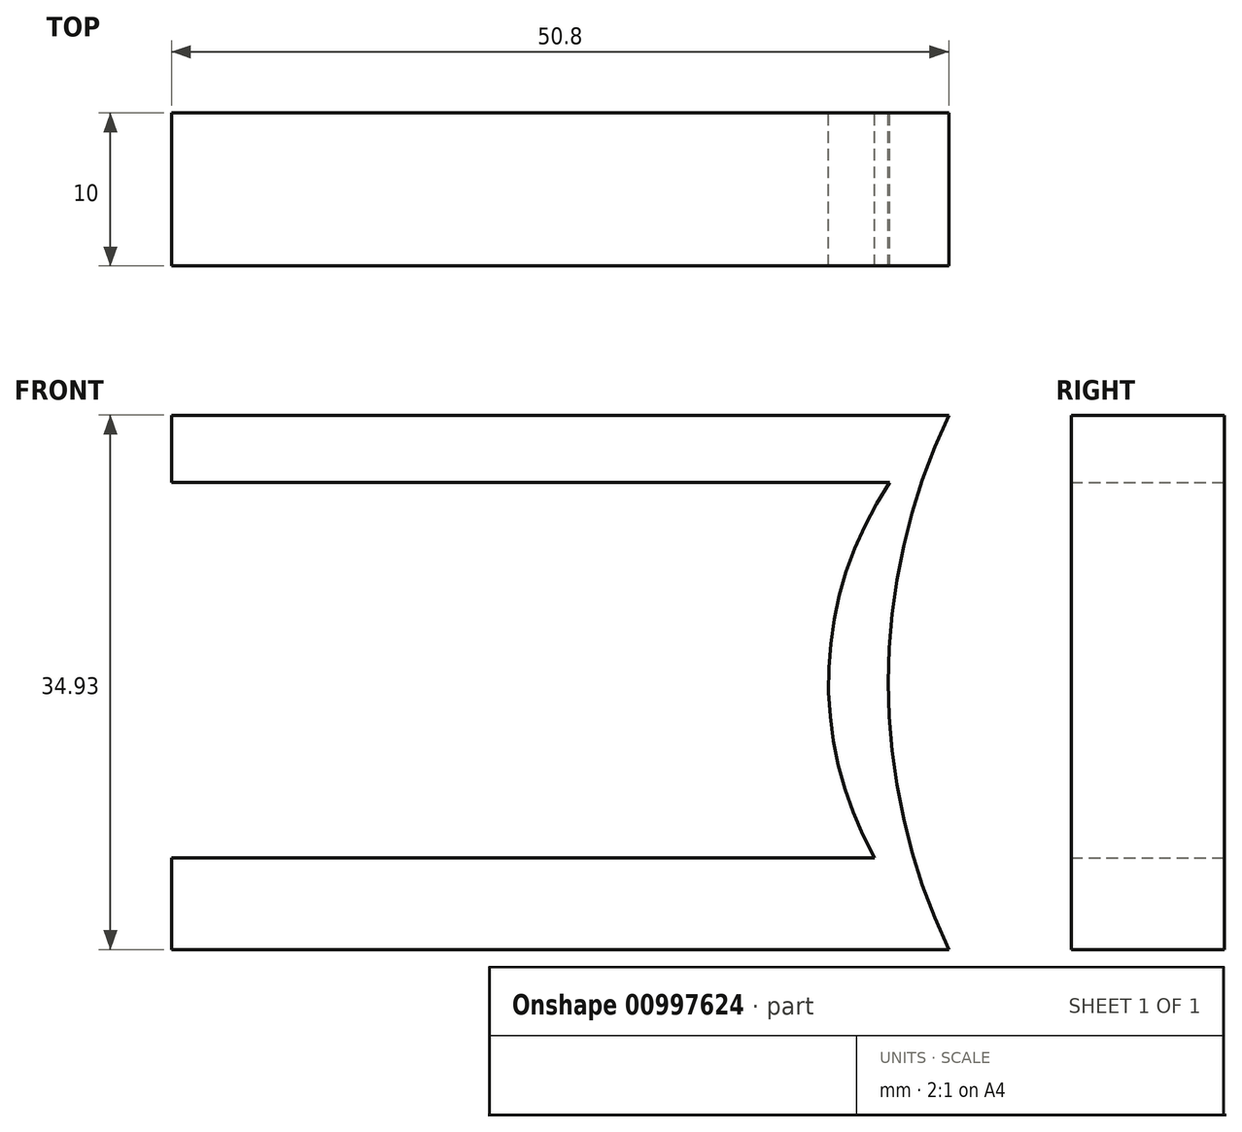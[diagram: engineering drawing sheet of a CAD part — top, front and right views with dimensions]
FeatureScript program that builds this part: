
annotation { "Feature Type Name" : "Feature", "Feature Type Description" : "" }
export const myFeature = defineFeature(function(context is Context, id is Id, definition is map)
    precondition{}
    {
        {
            var Q0;
            Q0=qCreatedBy(makeId("Front.planeOp"),FACE);
            var sketch = newSketch(context, id + "F0", { "sketchPlane" : qUnion([Q0])});
            skLineSegment(sketch, "E0", {"start": v(-49.37, 34.93) * mm, "end": v(1.43, 34.93) * mm});
            skLineSegment(sketch, "E1", {"start": v(-49.37, 0) * mm, "end": v(1.43, 0) * mm});
            skArc(sketch, "E2", {"start": v(1.43, 34.92) * mm, "mid": v(-6.43, 17.46) * mm, "end": v(1.43, 0) * mm});
            skArc(sketch, "E3", {"start": v(1.43, 34.92) * mm, "mid": v(-2.52, 17.46) * mm, "end": v(1.43, 0) * mm});
            skLineSegment(sketch, "E4", {"start": v(-2.43, 30.53) * mm, "end": v(-49.37, 30.53) * mm});
            skLineSegment(sketch, "E5", {"start": v(-49.37, 30.53) * mm, "end": v(-49.37, 34.93) * mm});
            skLineSegment(sketch, "E6", {"start": v(-49.37, 0) * mm, "end": v(-49.37, 6) * mm});
            skLineSegment(sketch, "E7", {"start": v(-49.37, 6) * mm, "end": v(-3.42, 6) * mm});
            skSolve(sketch);
        }
        {
            var Q0;
            {var subQ0=sQuery(id+"F0.wireOp",EDGE,"E0");Q0=makeQuery(id+"F0.imprint","IMPRINT",FACE,{"disambiguationData":[TD([[makeQuery(id+"F0.imprint","IMPRINT",EDGE,{"derivedFrom":subQ0}),-1.0]])]});}
            var Q1;
            {var subQ0=sQuery(id+"F0.wireOp",EDGE,"E1");Q1=makeQuery(id+"F0.imprint","IMPRINT",FACE,{"disambiguationData":[TD([[makeQuery(id+"F0.imprint","IMPRINT",EDGE,{"derivedFrom":subQ0}),1.0]])]});}
            var Q2;
            {var subQ0=sQuery(id+"F0.wireOp",EDGE,"E3");Q2=makeQuery(id+"F0.imprint","IMPRINT",FACE,{"disambiguationData":[TD([[makeQuery(id+"F0.imprint","IMPRINT",EDGE,{"derivedFrom":subQ0}),-1.0]])]});}
            extrude(context, id + "F1", {"entities" : qUnion([Q0, Q1, Q2]), "depth" : 10 * mm, "offsetDistance" : 25.4 * mm});
        }
    });
